# Revit family: NXSP_Series
name_source: partatom
category: Data Devices
units: mm (PartAtom-declared; Revit-internal decimal feet)

## family parameters
Cut with Voids When Loaded = No
Host = Face
Maintain Annotation Orientation = No
OmniClass Number = 23.85.50.17.11
OmniClass Title = Computer Network Equipment
Part Type = Normal
Room Calculation Point = No
Round Connector Dimension = Use Diameter
Shared = No

## types (1)
- NXSP Series
    Apparent Load = 0 VA
    Assembly Code = D5030
    Capacity = Four SmartPORTs, eight Smart Switches max per port
    Connector Description 1 = Power Supply
    Connector Description 2 = Data
    Default Elevation = 48 "
    Description = SmartPORT™ Module
    Electrical = Class 2, 24VDC, 250 mA max current available for connected devices, Plugs into NXHDI for power and network connection
    Load Classification = Other
    Manufacturer = NX Lighting Controls
    Model = NXSP SERIES
    Mounting = DIN rail, requires NXENC-D accessory enclosure
    Network Interface = Connects to the  network through the NXHDI Device; Network Interface Module required
    Number of Poles = 1
    Operating Environment = Indoor use only
    Operating Temperature = 32° to 104° (0° to 40° C)
    Passive Infrared = Dual-element pyrometer and 12-element cylindrical RhinoTuff lens
    Power Factor = 1
    Product Material = Gray
    Programming = Allows configuration and programming of the attached devices via web browser interface served from the Area Controller
    Relative humidity = 0% to 95% (non condensing)
    Type Comments = Data Devices
    URL = https://www.currentlighting.com
    Voltage = 120 V
    Warranty = Five-year limited
    Weight = 0.17 kg

## geometry (parser evidence)
native form markers: Sweep x4
no freeform markers — native parametric forms only
